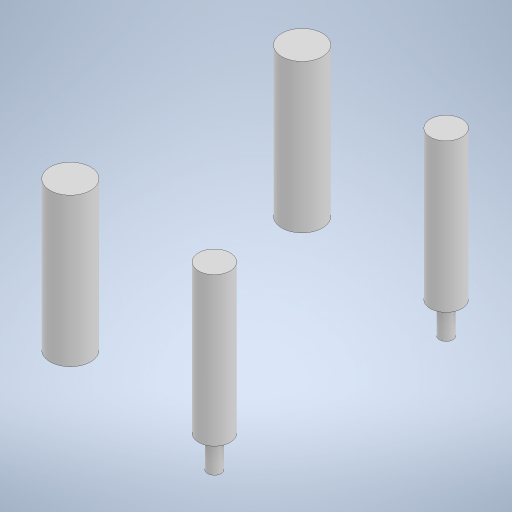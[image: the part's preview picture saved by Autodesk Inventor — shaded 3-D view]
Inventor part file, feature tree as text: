
AUTODESK INVENTOR PART (.ipt)
format: ipt  version: 2024 (Build 280153000, 153)  size: 264,704 bytes
history: native  units: mm
features: sketch x5, extrude x4
ambient origin geometry x8: Origin, YZ Plane, XZ Plane, XY Plane, X Axis, Y Axis, Z Axis, Center Point
bodies: Solid1 (feature_tree)
feature tree (9):
  extrude  "Extrusion1"  Depth=6.5mm
  extrude  "Extrusion2"  Depth=9.0mm
  sketch  "Sketch3"  dims[d4=7.0mm d5=7.0mm]
  extrude  "Extrusion3"  Depth=7.0mm
  extrude  "Extrusion4"  Depth=32.0mm
  sketch  "Sketch1"  dims[d0=9.0mm d1=6.5mm]
  sketch  "Sketch2"  dims[d2=6.5mm d3=9.0mm]
  sketch  "Sketch4"  dims[d6=51.5mm d7=32.0mm]
  sketch  "Sketch5"  dims[d8=6.0mm d9=0.0mm d10=3.0mm d11=3.0mm d12=7.0mm d13=0.0mm d14=7.0mm d15=0.0mm d16=20.0mm d17=0.0mm d18=7.0mm d19=7.0mm d20=9.0mm d21=9.0mm]
